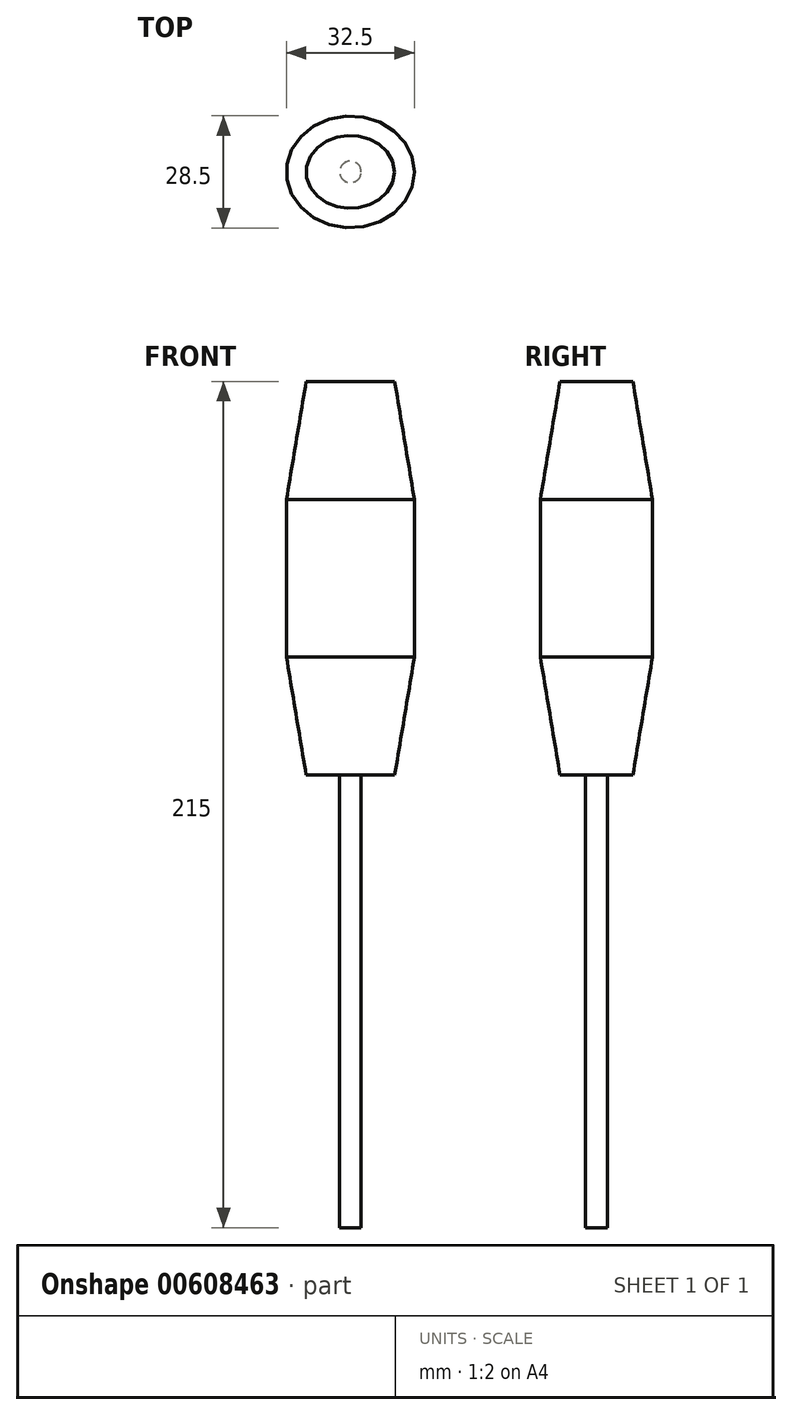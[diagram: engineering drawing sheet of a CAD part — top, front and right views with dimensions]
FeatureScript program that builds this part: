
annotation { "Feature Type Name" : "Feature", "Feature Type Description" : "" }
export const myFeature = defineFeature(function(context is Context, id is Id, definition is map)
    precondition{}
    {
        {
            var Q0;
            Q0=qCreatedBy(makeId("Top.planeOp"),FACE);
            var sketch = newSketch(context, id + "F0", { "sketchPlane" : qUnion([Q0])});
            skEllipse(sketch, "E0", {"center": v(0, 0) * mm, "majorRadius": 16.25 * mm, "minorRadius": 14.25 * mm, "majorAxis": v(1, 0)});
            skSolve(sketch);
        }
        {
            var Q0;
            Q0=makeQuery(id+"F0.imprint","IMPRINT",FACE,{"disambiguationData":[TD([[makeQuery(id+"F0.imprint","IMPRINT",EDGE,{"derivedFrom":sQuery(id+"F0.wireOp",EDGE,"E0")}),1.0]])]});
            extrude(context, id + "F1", {"entities" : qUnion([Q0]), "depth" : 100 * mm, "offsetDistance" : 25 * mm});
        }
        {
            var Q0;
            Q0=makeQuery(id+"F1.opExtrude","CAP_FACE",FACE,{"disambiguationData":[OSD([sQuery(id+"F0.wireOp",EDGE,"E0")])],"isStart":true});
            var sketch = newSketch(context, id + "F2", { "sketchPlane" : qUnion([Q0])});
            skCircle(sketch, "E1", {"center": v(0, 0) * mm, "radius": 2.75 * mm});
            skSolve(sketch);
        }
        {
            var Q0;
            Q0 = qSketchRegion(id + "F2", true);
            extrude(context, id + "F3", {"entities" : qUnion([Q0]), "operationType" : NewBodyOperationType.ADD, "depth" : 115 * mm, "offsetDistance" : 25 * mm});
        }
        {
            var Q0;
            Q0=makeQuery(id+"F1.opExtrude","CAP_EDGE",EDGE,{"disambiguationData":[OSD([sQuery(id+"F0.wireOp",EDGE,"E0")])],"isStart":false});
            var Q1;
            Q1=makeQuery(id+"F1.opExtrude","CAP_EDGE",EDGE,{"disambiguationData":[OSD([sQuery(id+"F0.wireOp",EDGE,"E0")])],"isStart":true});
            chamfer(context, id + "F4", {"entities" : qUnion([Q0, Q1]), "chamferType" : ChamferType.TWO_OFFSETS, "width1" : 5 * mm, "oppositeDirection" : false, "width2" : 30 * mm, "tangentPropagation" : true});
        }
    });
